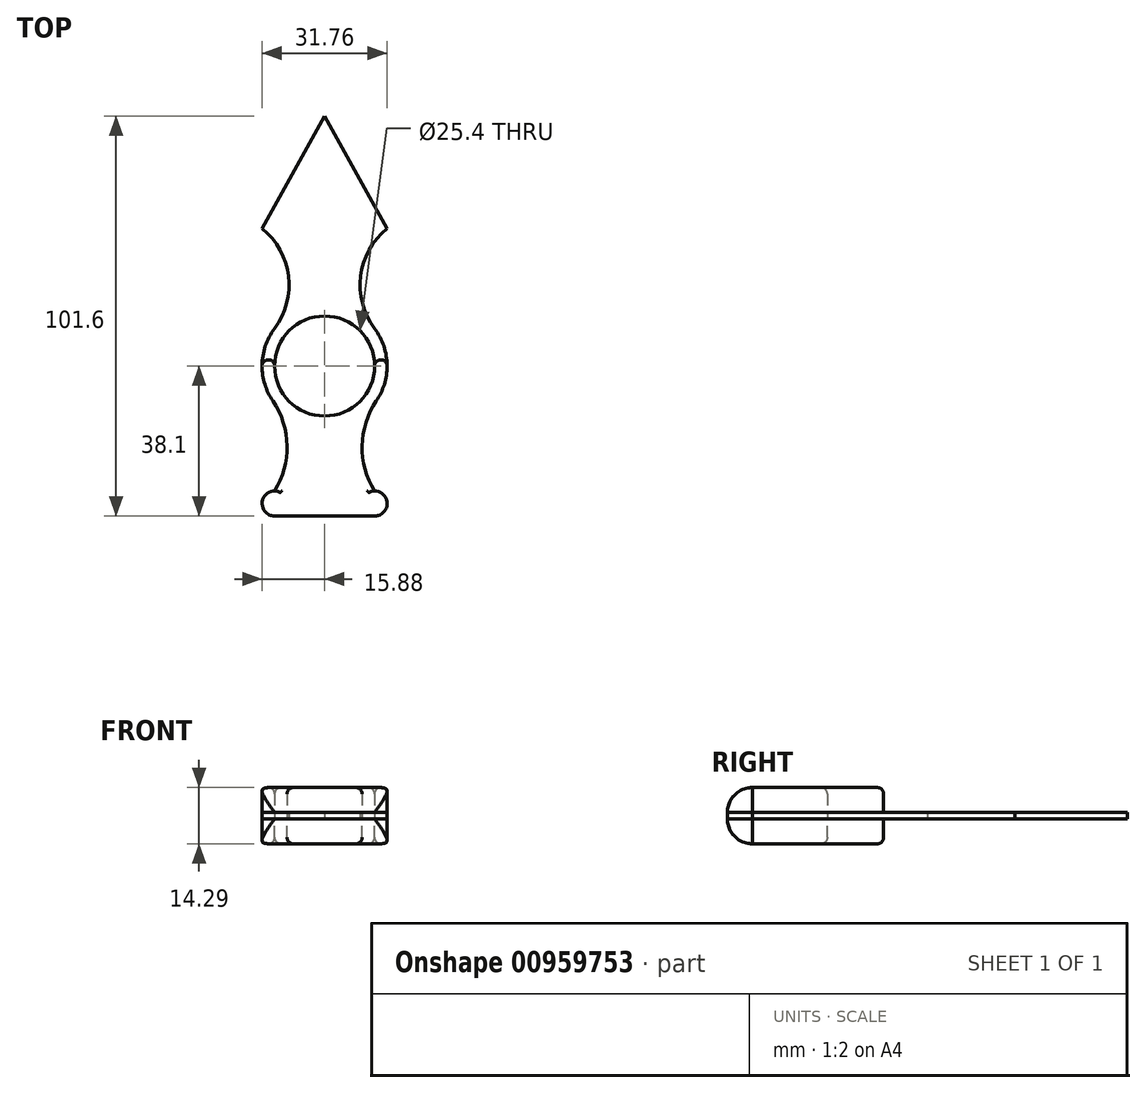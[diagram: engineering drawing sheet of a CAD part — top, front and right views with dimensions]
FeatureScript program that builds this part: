
annotation { "Feature Type Name" : "Feature", "Feature Type Description" : "" }
export const myFeature = defineFeature(function(context is Context, id is Id, definition is map)
    precondition{}
    {
        {
            var Q0;
            Q0=qCreatedBy(makeId("Top.planeOp"),FACE);
            var sketch = newSketch(context, id + "F0", { "sketchPlane" : qUnion([Q0])});
            skCircle(sketch, "E0", {"center": v(0, 0) * mm, "radius": 12.7 * mm});
            skPoint(sketch, "E1", {"position": v(0, 63.5) * mm});
            skArc(sketch, "E2", {"start": v(13.14, -8.91) * mm, "mid": v(0, 15.88) * mm, "end": v(-13.14, -8.91) * mm});
            skArc(sketch, "E3", {"start": v(15.87, 34.92) * mm, "mid": v(9.16, 22.87) * mm, "end": v(12.7, 9.52) * mm});
            skPoint(sketch, "E4", {"position": v(12.7, 0) * mm});
            skLineSegment(sketch, "E5", {"start": v(0, 63.5) * mm, "end": v(0, -38.1) * mm, "construction": true});
            skLineSegment(sketch, "E6", {"start": v(15.87, 34.92) * mm, "end": v(0, 34.92) * mm, "construction": true});
            skPoint(sketch, "E7", {"position": v(15.88, 0) * mm});
            skLineSegment(sketch, "E8", {"start": v(0, -38.1) * mm, "end": v(12.7, -38.1) * mm});
            skArc(sketch, "E9", {"start": v(12.7, -38.1) * mm, "mid": v(15.88, -34.93) * mm, "end": v(12.7, -31.75) * mm});
            skArc(sketch, "E10", {"start": v(13.14, -8.91) * mm, "mid": v(9.53, -20.27) * mm, "end": v(12.7, -31.75) * mm});
            skLineSegment(sketch, "E11.MirrorCS", {"start": v(0, -38.1) * mm, "end": v(-12.7, -38.1) * mm});
            skArc(sketch, "E12.MirrorCS", {"start": v(-12.7, -38.1) * mm, "mid": v(-15.88, -34.93) * mm, "end": v(-12.7, -31.75) * mm});
            skArc(sketch, "E13.MirrorCS", {"start": v(-13.14, -8.91) * mm, "mid": v(-9.53, -20.27) * mm, "end": v(-12.7, -31.75) * mm});
            skArc(sketch, "E14.MirrorCS", {"start": v(-15.87, 34.92) * mm, "mid": v(-9.16, 22.87) * mm, "end": v(-12.7, 9.53) * mm});
            skPoint(sketch, "E15.MirrorCS.end.orphan", {"position": v(-15.87, 34.92) * mm});
            skLineSegment(sketch, "E16", {"start": v(-15.87, 34.92) * mm, "end": v(0, 63.5) * mm});
            skLineSegment(sketch, "E17", {"start": v(0, 63.5) * mm, "end": v(0, 63.5) * mm});
            skLineSegment(sketch, "E18", {"start": v(15.87, 34.92) * mm, "end": v(0, 63.5) * mm});
            skSolve(sketch);
        }
        {
            var Q0;
            {var subQ0=sQuery(id+"F0.wireOp",EDGE,"E3");Q0=makeQuery(id+"F0.imprint","IMPRINT",FACE,{"disambiguationData":[TD([[makeQuery(id+"F0.imprint","IMPRINT",EDGE,{"derivedFrom":subQ0}),-1.0]])]});}
            extrude(context, id + "F1", {"entities" : qUnion([Q0]), "depth" : 1.59 * mm, "offsetDistance" : 25.4 * mm});
        }
        {
            var Q0;
            Q0=makeQuery(id+"F0.imprint","IMPRINT",FACE,{"disambiguationData":[TD([[makeQuery(id+"F0.imprint","IMPRINT",EDGE,{"derivedFrom":sQuery(id+"F0.wireOp",EDGE,"E0")}),-1.0]])]});
            extrude(context, id + "F2", {"entities" : qUnion([Q0]), "operationType" : NewBodyOperationType.ADD, "depth" : 1.59 * mm, "offsetDistance" : 25.4 * mm});
        }
        {
            var Q0;
            {var subQ0=sQuery(id+"F0.wireOp",EDGE,"E2");Q0=makeQuery(id+"F2.boolean.opBoolean","MERGE",FACE,{"derivedFrom":[makeQuery(id+"F1.opExtrude","CAP_FACE",FACE,{"disambiguationData":[OSD([subQ0,sQuery(id+"F0.wireOp",EDGE,"E3"),sQuery(id+"F0.wireOp",EDGE,"E14.MirrorCS"),sQuery(id+"F0.wireOp",EDGE,"E16"),sQuery(id+"F0.wireOp",EDGE,"E18")])],"isStart":false}),makeQuery(id+"F2.opExtrude","CAP_FACE",FACE,{"disambiguationData":[OSD([sQuery(id+"F0.wireOp",EDGE,"E0"),subQ0,sQuery(id+"F0.wireOp",EDGE,"E8"),sQuery(id+"F0.wireOp",EDGE,"E9"),sQuery(id+"F0.wireOp",EDGE,"E10"),sQuery(id+"F0.wireOp",EDGE,"E11.MirrorCS"),sQuery(id+"F0.wireOp",EDGE,"E12.MirrorCS"),sQuery(id+"F0.wireOp",EDGE,"E13.MirrorCS")])],"isStart":false})]});}
            var sketch = newSketch(context, id + "F3", { "sketchPlane" : qUnion([Q0])});
            skArc(sketch, "E19", {"start": v(-12.7, 0) * mm, "mid": v(-14.29, 1.59) * mm, "end": v(-15.88, 0) * mm});
            skArc(sketch, "E20", {"start": v(15.88, 0) * mm, "mid": v(14.29, 1.59) * mm, "end": v(12.7, 0) * mm});
            skSolve(sketch);
        }
        {
            var Q0;
            {var subQ4=sQuery(id+"F3.wireOp",EDGE,"E19");Q0=makeQuery(id+"F3.imprint","IMPRINT",FACE,{"disambiguationData":[TD([[makeQuery(id+"F3.imprint","IMPRINT",EDGE,{"derivedFrom":subQ4}),1.0]])]});}
            extrude(context, id + "F4", {"entities" : qUnion([Q0]), "depth" : 6.35 * mm, "offsetDistance" : 25.4 * mm});
        }
        {
            var Q0;
            {var subQ0=sQuery(id+"F0.wireOp",EDGE,"E2");Q0=makeQuery(id+"F2.boolean.opBoolean","MERGE",FACE,{"derivedFrom":[makeQuery(id+"F1.opExtrude","CAP_FACE",FACE,{"disambiguationData":[OSD([subQ0,sQuery(id+"F0.wireOp",EDGE,"E3"),sQuery(id+"F0.wireOp",EDGE,"E14.MirrorCS"),sQuery(id+"F0.wireOp",EDGE,"E16"),sQuery(id+"F0.wireOp",EDGE,"E18")])],"isStart":true}),makeQuery(id+"F2.opExtrude","CAP_FACE",FACE,{"disambiguationData":[OSD([sQuery(id+"F0.wireOp",EDGE,"E0"),subQ0,sQuery(id+"F0.wireOp",EDGE,"E8"),sQuery(id+"F0.wireOp",EDGE,"E9"),sQuery(id+"F0.wireOp",EDGE,"E10"),sQuery(id+"F0.wireOp",EDGE,"E11.MirrorCS"),sQuery(id+"F0.wireOp",EDGE,"E12.MirrorCS"),sQuery(id+"F0.wireOp",EDGE,"E13.MirrorCS")])],"isStart":true})]});}
            var sketch = newSketch(context, id + "F5", { "sketchPlane" : qUnion([Q0])});
            skArc(sketch, "E21", {"start": v(12.7, 0) * mm, "mid": v(14.29, -1.59) * mm, "end": v(15.88, 0) * mm});
            skArc(sketch, "E22", {"start": v(-15.88, 0) * mm, "mid": v(-14.29, -1.59) * mm, "end": v(-12.7, 0) * mm});
            skSolve(sketch);
        }
        {
            var Q0;
            {var subQ4=sQuery(id+"F5.wireOp",EDGE,"E21");Q0=makeQuery(id+"F5.imprint","IMPRINT",FACE,{"disambiguationData":[TD([[makeQuery(id+"F5.imprint","IMPRINT",EDGE,{"derivedFrom":subQ4}),1.0]])]});}
            extrude(context, id + "F6", {"entities" : qUnion([Q0]), "depth" : 6.35 * mm, "offsetDistance" : 25.4 * mm});
        }
        {
            var Q0;
            Q0=makeQuery(id+"F6.opExtrude","CAP_EDGE",EDGE,{"disambiguationData":[OSD([sQuery(id+"F0.wireOp",EDGE,"E8"),sQuery(id+"F0.wireOp",EDGE,"E11.MirrorCS")])],"isStart":false});
            var Q1;
            Q1=makeQuery(id+"F4.opExtrude","CAP_EDGE",EDGE,{"disambiguationData":[OSD([sQuery(id+"F0.wireOp",EDGE,"E8"),sQuery(id+"F0.wireOp",EDGE,"E11.MirrorCS")])],"isStart":false});
            fillet(context, id + "F7", {"entities" : qUnion([Q0, Q1]), "radius" : 6.35 * mm, "allowEdgeOverflow" : false});
        }
        {
            var Q0;
            {var subQ0=sQuery(id+"F0.wireOp",EDGE,"E10");var subQ1=sQuery(id+"F0.wireOp",EDGE,"E2");var subQ2=sQuery(id+"F0.wireOp",EDGE,"E3");var subQ3=makeQuery(id+"F2.boolean.opBoolean","SPLIT",EDGE,{"disambiguationData":[TD([makeQuery(id+"FSpSUOPilyjBolP_1.opChamfer","BLEND_FACE",FACE,{"disambiguationData":[OSD([subQ2])]})])],"derivedFrom":makeQuery(id+"F2.opExtrude","CAP_EDGE",EDGE,{"disambiguationData":[OSD([subQ1])],"isStart":true})});Q0=makeQuery(id+"F6.opExtrude","CAP_EDGE",EDGE,{"disambiguationData":[OSD([subQ1]),TDD([makeQuery(id+"F5.imprint","IMPRINT",EDGE,{"disambiguationData":[TD([[makeQuery(id+"F5.imprint","INTERSECT",VERTEX,{"derivedFrom":[makeQuery(id+"F2.opExtrude","CAP_EDGE",EDGE,{"disambiguationData":[OSD([subQ0])],"isStart":true}),subQ3]}),-1.0]])],"derivedFrom":subQ3})])],"isStart":false});}
            var Q1;
            Q1=makeQuery(id+"F6.opExtrude","CAP_EDGE",EDGE,{"disambiguationData":[OSD([sQuery(id+"F0.wireOp",EDGE,"E0")])],"isStart":false});
            var Q2;
            {var subQ0=sQuery(id+"F0.wireOp",EDGE,"E13.MirrorCS");var subQ1=sQuery(id+"F0.wireOp",EDGE,"E2");var subQ2=sQuery(id+"F0.wireOp",EDGE,"E14.MirrorCS");var subQ3=makeQuery(id+"F2.boolean.opBoolean","SPLIT",EDGE,{"disambiguationData":[TD([makeQuery(id+"FSpSUOPilyjBolP_1.opChamfer","BLEND_FACE",FACE,{"disambiguationData":[OSD([subQ2])]})])],"derivedFrom":makeQuery(id+"F2.opExtrude","CAP_EDGE",EDGE,{"disambiguationData":[OSD([subQ1])],"isStart":true})});Q2=makeQuery(id+"F6.opExtrude","CAP_EDGE",EDGE,{"disambiguationData":[OSD([subQ1]),TDD([makeQuery(id+"F5.imprint","IMPRINT",EDGE,{"disambiguationData":[TD([[makeQuery(id+"F5.imprint","INTERSECT",VERTEX,{"derivedFrom":[makeQuery(id+"F2.opExtrude","CAP_EDGE",EDGE,{"disambiguationData":[OSD([subQ0])],"isStart":true}),subQ3]}),1.0]])],"derivedFrom":subQ3})])],"isStart":false});}
            var Q3;
            {var subQ0=sQuery(id+"F0.wireOp",EDGE,"E2");var subQ1=sQuery(id+"F0.wireOp",EDGE,"E10");var subQ2=sQuery(id+"F0.wireOp",EDGE,"E3");var subQ3=makeQuery(id+"F2.boolean.opBoolean","SPLIT",EDGE,{"disambiguationData":[TD([makeQuery(id+"FuxqoHOueu8lmOZ_1.opChamfer","BLEND_FACE",FACE,{"disambiguationData":[OSD([subQ2])]})])],"derivedFrom":makeQuery(id+"F2.opExtrude","CAP_EDGE",EDGE,{"disambiguationData":[OSD([subQ0])],"isStart":false})});Q3=makeQuery(id+"F4.opExtrude","CAP_EDGE",EDGE,{"disambiguationData":[OSD([subQ0]),TDD([makeQuery(id+"F3.imprint","IMPRINT",EDGE,{"disambiguationData":[TD([[makeQuery(id+"F3.imprint","INTERSECT",VERTEX,{"derivedFrom":[makeQuery(id+"F2.opExtrude","CAP_EDGE",EDGE,{"disambiguationData":[OSD([subQ1])],"isStart":false}),subQ3]}),-1.0]])],"derivedFrom":subQ3})])],"isStart":false});}
            var Q4;
            Q4=makeQuery(id+"F4.opExtrude","CAP_EDGE",EDGE,{"disambiguationData":[OSD([sQuery(id+"F0.wireOp",EDGE,"E0")])],"isStart":false});
            var Q5;
            {var subQ0=sQuery(id+"F0.wireOp",EDGE,"E2");var subQ1=sQuery(id+"F0.wireOp",EDGE,"E13.MirrorCS");var subQ2=sQuery(id+"F0.wireOp",EDGE,"E14.MirrorCS");var subQ3=makeQuery(id+"F2.boolean.opBoolean","SPLIT",EDGE,{"disambiguationData":[TD([makeQuery(id+"FuxqoHOueu8lmOZ_1.opChamfer","BLEND_FACE",FACE,{"disambiguationData":[OSD([subQ2])]})])],"derivedFrom":makeQuery(id+"F2.opExtrude","CAP_EDGE",EDGE,{"disambiguationData":[OSD([subQ0])],"isStart":false})});Q5=makeQuery(id+"F4.opExtrude","CAP_EDGE",EDGE,{"disambiguationData":[OSD([subQ0]),TDD([makeQuery(id+"F3.imprint","IMPRINT",EDGE,{"disambiguationData":[TD([[makeQuery(id+"F3.imprint","INTERSECT",VERTEX,{"derivedFrom":[makeQuery(id+"F2.opExtrude","CAP_EDGE",EDGE,{"disambiguationData":[OSD([subQ1])],"isStart":false}),subQ3]}),1.0]])],"derivedFrom":subQ3})])],"isStart":false});}
            fillet(context, id + "F8", {"entities" : qUnion([Q0, Q1, Q2, Q3, Q4, Q5]), "radius" : 1.59 * mm, "tangentPropagation" : true, "allowEdgeOverflow" : false});
        }
    });
